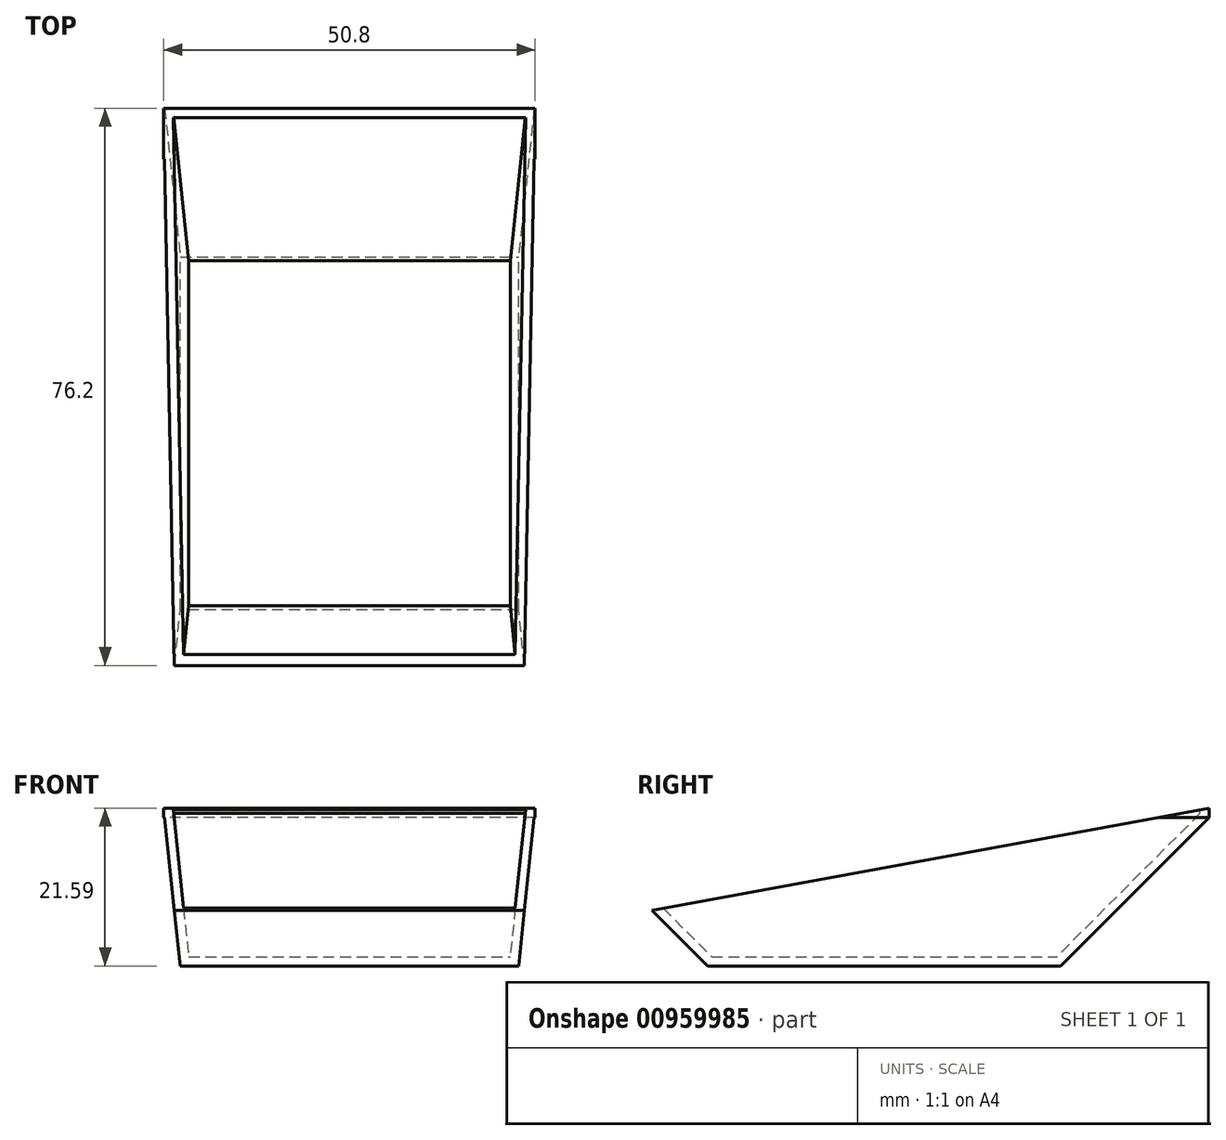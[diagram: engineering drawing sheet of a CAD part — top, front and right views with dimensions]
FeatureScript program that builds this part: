
annotation { "Feature Type Name" : "Feature", "Feature Type Description" : "" }
export const myFeature = defineFeature(function(context is Context, id is Id, definition is map)
    precondition{}
    {
        {
            var Q0;
            Q0=qCreatedBy(makeId("Top.planeOp"),FACE);
            var sketch = newSketch(context, id + "F0", { "sketchPlane" : qUnion([Q0])});
            skLineSegment(sketch, "E0.bottom", {"start": v(-25.4, 38.1) * mm, "end": v(25.4, 38.1) * mm});
            skLineSegment(sketch, "E0.top", {"start": v(-25.4, -38.1) * mm, "end": v(25.4, -38.1) * mm});
            skLineSegment(sketch, "E0.left", {"start": v(-25.4, 38.1) * mm, "end": v(-25.4, -38.1) * mm});
            skLineSegment(sketch, "E0.right", {"start": v(25.4, 38.1) * mm, "end": v(25.4, -38.1) * mm});
            skPoint(sketch, "E0.middle", {"position": v(0, 0) * mm});
            skSolve(sketch);
        }
        {
            var Q0;
            Q0 = qSketchRegion(id + "F0", true);
            extrude(context, id + "F1", {"entities" : qUnion([Q0]), "depth" : 21.59 * mm, "offsetDistance" : 25.4 * mm});
        }
        {
            var Q0;
            Q0=makeQuery(id+"F1.opExtrude","CAP_EDGE",EDGE,{"disambiguationData":[OSD([sQuery(id+"F0.wireOp",EDGE,"E0.bottom")])],"isStart":true});
            chamfer(context, id + "F2", {"entities" : qUnion([Q0]), "width" : 20.32 * mm, "tangentPropagation" : true});
        }
        {
            var Q0;
            Q0=makeQuery(id+"F1.opExtrude","CAP_EDGE",EDGE,{"disambiguationData":[OSD([sQuery(id+"F0.wireOp",EDGE,"E0.top")])],"isStart":true});
            chamfer(context, id + "F3", {"entities" : qUnion([Q0]), "width" : 7.62 * mm, "tangentPropagation" : true});
        }
        {
            var Q0;
            Q0=makeQuery(id+"F1.opExtrude","SWEPT_FACE",FACE,{"disambiguationData":[OSD([sQuery(id+"F0.wireOp",EDGE,"E0.left")])]});
            var sketch = newSketch(context, id + "F4", { "sketchPlane" : qUnion([Q0])});
            skLineSegment(sketch, "E1", {"start": v(-38.1, 21.59) * mm, "end": v(38.1, 7.62) * mm});
            skLineSegment(sketch, "E2.0", {"start": v(-38.1, 21.59) * mm, "end": v(38.1, 21.59) * mm});
            skLineSegment(sketch, "E3.0", {"start": v(38.1, 21.59) * mm, "end": v(38.1, 7.62) * mm});
            skSolve(sketch);
        }
        {
            var Q0;
            Q0=makeQuery(id+"F4.imprint","IMPRINT",FACE,{"disambiguationData":[TD([[makeQuery(id+"F4.imprint","IMPRINT",EDGE,{"derivedFrom":sQuery(id+"F4.wireOp",EDGE,"E1")}),1.0]])]});
            extrude(context, id + "F5", {"entities" : qUnion([Q0]), "operationType" : NewBodyOperationType.REMOVE, "endBound" : BoundingType.THROUGH_ALL, "oppositeDirection" : true, "depth" : 25.4 * mm, "offsetDistance" : 25.4 * mm});
        }
        {
            var Q0;
            Q0=makeQuery(id+"F1.opExtrude","SWEPT_FACE",FACE,{"disambiguationData":[OSD([sQuery(id+"F0.wireOp",EDGE,"E0.bottom")])]});
            var sketch = newSketch(context, id + "F6", { "sketchPlane" : qUnion([Q0])});
            skLineSegment(sketch, "E4", {"start": v(-25.4, 21.6) * mm, "end": v(-23.13, 0) * mm});
            skLineSegment(sketch, "E5.0", {"start": v(25.4, 21.59) * mm, "end": v(-25.4, 21.59) * mm});
            skLineSegment(sketch, "E6", {"start": v(25.4, 21.6) * mm, "end": v(23.13, 0) * mm});
            skLineSegment(sketch, "E7", {"start": v(-23.13, 0) * mm, "end": v(23.13, 0) * mm});
            skLineSegment(sketch, "E8", {"start": v(-25.4, 21.6) * mm, "end": v(-25.4, 0) * mm});
            skLineSegment(sketch, "E9", {"start": v(-25.4, 0) * mm, "end": v(-23.13, 0) * mm});
            skLineSegment(sketch, "E10", {"start": v(25.4, 21.59) * mm, "end": v(25.4, 0) * mm});
            skLineSegment(sketch, "E11", {"start": v(23.13, 0) * mm, "end": v(25.4, 0) * mm});
            skSolve(sketch);
        }
        {
            var Q0;
            {var subQ0=sQuery(id+"F6.wireOp",EDGE,"E11");Q0=makeQuery(id+"F6.imprint","IMPRINT",FACE,{"disambiguationData":[TD([[makeQuery(id+"F6.imprint","IMPRINT",EDGE,{"derivedFrom":subQ0}),1.0]])]});}
            var Q1;
            {var subQ0=sQuery(id+"F6.wireOp",EDGE,"E9");Q1=makeQuery(id+"F6.imprint","IMPRINT",FACE,{"disambiguationData":[TD([[makeQuery(id+"F6.imprint","IMPRINT",EDGE,{"derivedFrom":subQ0}),1.0]])]});}
            extrude(context, id + "F7", {"entities" : qUnion([Q0, Q1]), "operationType" : NewBodyOperationType.REMOVE, "endBound" : BoundingType.THROUGH_ALL, "oppositeDirection" : true, "depth" : 25.4 * mm, "offsetDistance" : 25.4 * mm});
        }
        {
            var Q0;
            Q0=makeQuery(id+"F5.boolean.opBoolean","COPY",FACE,{"derivedFrom":makeQuery(id+"F5.opExtrude","SWEPT_FACE",FACE,{"disambiguationData":[OSD([sQuery(id+"F4.wireOp",EDGE,"E1")])]})});
            shell(context, id + "F8", {"entities" : qUnion([Q0]), "thickness" : 1.27 * mm});
        }
    });
